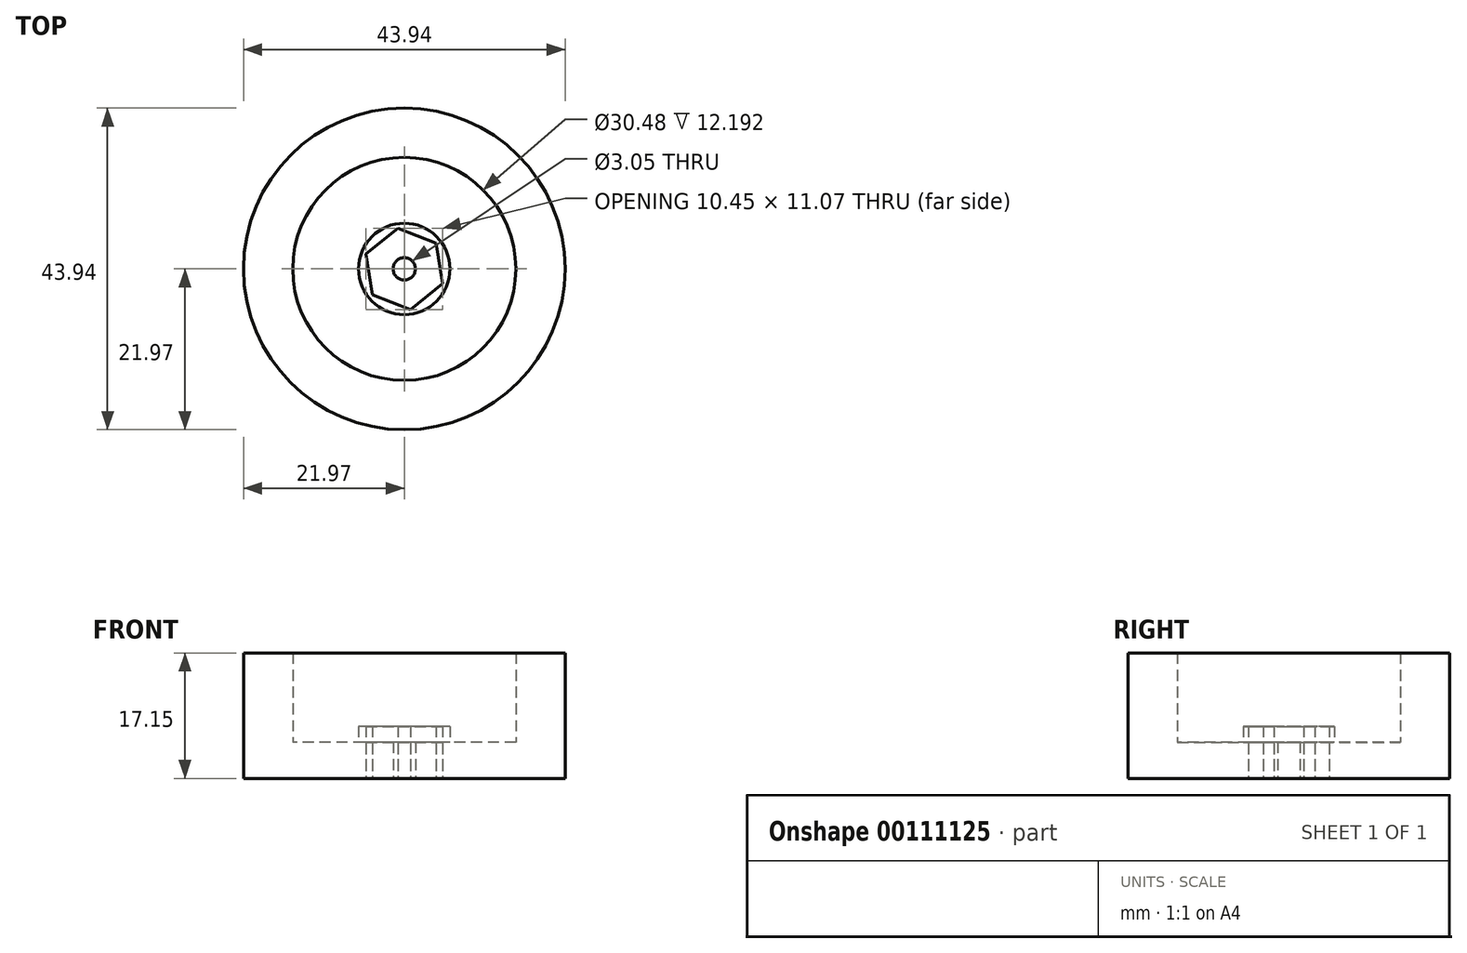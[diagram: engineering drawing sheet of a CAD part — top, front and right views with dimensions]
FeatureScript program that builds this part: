
annotation { "Feature Type Name" : "Feature", "Feature Type Description" : "" }
export const myFeature = defineFeature(function(context is Context, id is Id, definition is map)
    precondition{}
    {
        {
            var Q0;
            Q0=qCreatedBy(makeId("Top.planeOp"),FACE);
            var sketch = newSketch(context, id + "F0", { "sketchPlane" : qUnion([Q0])});
            skCircle(sketch, "E0.cCircle", {"center": v(0, 0) * mm, "radius": 4.85 * mm, "construction": true});
            skLineSegment(sketch, "E0.0", {"start": v(-5.22, 2.02) * mm, "end": v(-0.86, 5.54) * mm});
            skLineSegment(sketch, "E0.1", {"start": v(-0.86, 5.54) * mm, "end": v(4.36, 3.51) * mm});
            skLineSegment(sketch, "E0.2", {"start": v(4.36, 3.51) * mm, "end": v(5.22, -2.02) * mm});
            skLineSegment(sketch, "E0.3", {"start": v(5.22, -2.02) * mm, "end": v(0.86, -5.54) * mm});
            skLineSegment(sketch, "E0.4", {"start": v(0.86, -5.54) * mm, "end": v(-4.36, -3.51) * mm});
            skLineSegment(sketch, "E0.5", {"start": v(-4.36, -3.51) * mm, "end": v(-5.22, 2.02) * mm});
            skPoint(sketch, "E0.0.midPoint", {"position": v(-3.04, 3.78) * mm});
            skCircle(sketch, "E1", {"center": v(0, 0) * mm, "radius": 1.52 * mm});
            skCircle(sketch, "E2", {"center": v(0, 0) * mm, "radius": 6.24 * mm});
            skSolve(sketch);
        }
        {
            var Q0;
            Q0=makeQuery(id+"F0.imprint","IMPRINT",FACE,{"disambiguationData":[TD([[makeQuery(id+"F0.imprint","IMPRINT",EDGE,{"derivedFrom":sQuery(id+"F0.wireOp",EDGE,"E0.0")}),-1.0]])]});
            extrude(context, id + "F1", {"entities" : qUnion([Q0]), "depth" : 4.95 * mm});
        }
        {
            var Q0;
            Q0 = qSketchRegion(id + "F0", true);
            extrude(context, id + "F2", {"entities" : qUnion([Q0]), "depth" : 7.11 * mm});
        }
        {
            var Q0;
            Q0=qCreatedBy(makeId("Top.planeOp"),FACE);
            var sketch = newSketch(context, id + "F3", { "sketchPlane" : qUnion([Q0])});
            skCircle(sketch, "E3", {"center": v(0, 0) * mm, "radius": 5.86 * mm});
            skCircle(sketch, "E4", {"center": v(0, 0) * mm, "radius": 15.5 * mm});
            skSolve(sketch);
        }
        {
            var Q0;
            Q0 = qSketchRegion(id + "F3", true);
            extrude(context, id + "F4", {"entities" : qUnion([Q0]), "operationType" : NewBodyOperationType.ADD, "depth" : 4.95 * mm});
        }
        {
            var Q0;
            Q0=qCreatedBy(makeId("Top.planeOp"),FACE);
            var sketch = newSketch(context, id + "F5", { "sketchPlane" : qUnion([Q0])});
            skCircle(sketch, "E5", {"center": v(0, 0) * mm, "radius": 15.24 * mm});
            skCircle(sketch, "E6", {"center": v(0, 0) * mm, "radius": 21.97 * mm});
            skSolve(sketch);
        }
        {
            var Q0;
            Q0 = qSketchRegion(id + "F5", true);
            extrude(context, id + "F6", {"entities" : qUnion([Q0]), "operationType" : NewBodyOperationType.ADD, "depth" : 17.14 * mm});
        }
    });
